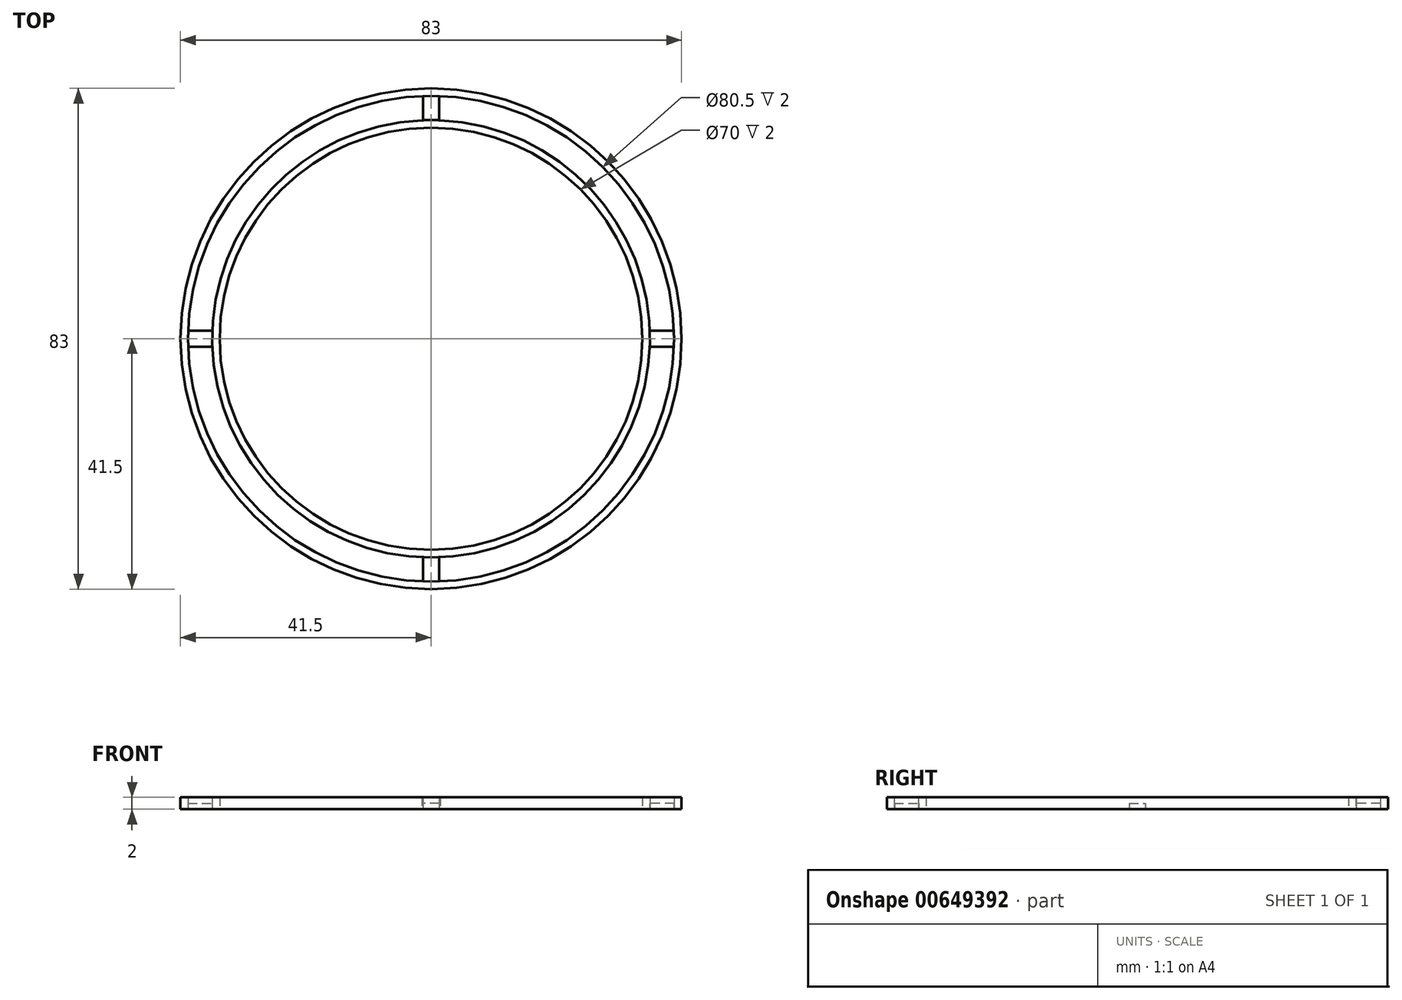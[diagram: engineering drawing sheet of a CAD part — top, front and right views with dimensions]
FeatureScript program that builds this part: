
annotation { "Feature Type Name" : "Feature", "Feature Type Description" : "" }
export const myFeature = defineFeature(function(context is Context, id is Id, definition is map)
    precondition{}
    {
        {
            var Q0;
            Q0=qCreatedBy(makeId("Top.planeOp"),FACE);
            var sketch = newSketch(context, id + "F0", { "sketchPlane" : qUnion([Q0])});
            skCircle(sketch, "E0", {"center": v(0, 0) * mm, "radius": 35 * mm});
            skCircle(sketch, "E1", {"center": v(0, 0) * mm, "radius": 36.25 * mm});
            skCircle(sketch, "E2", {"center": v(0, 0) * mm, "radius": 40.25 * mm});
            skCircle(sketch, "E3", {"center": v(0, 0) * mm, "radius": 41.5 * mm});
            skLineSegment(sketch, "E4.bottom", {"start": v(-1.52, 36.22) * mm, "end": v(1.61, 36.22) * mm});
            skLineSegment(sketch, "E4.top", {"start": v(-1.52, 41.47) * mm, "end": v(1.61, 41.47) * mm});
            skLineSegment(sketch, "E5.bottom", {"start": v(-1.33, 40.88) * mm, "end": v(1.33, 40.88) * mm});
            skLineSegment(sketch, "E5.top", {"start": v(-1.33, 35.2) * mm, "end": v(1.33, 35.2) * mm});
            skLineSegment(sketch, "E5.left", {"start": v(-1.33, 40.88) * mm, "end": v(-1.33, 35.2) * mm});
            skLineSegment(sketch, "E5.right", {"start": v(1.33, 40.88) * mm, "end": v(1.33, 35.2) * mm});
            skPoint(sketch, "E5.middle", {"position": v(0, 38.04) * mm});
            skLineSegment(sketch, "E6.1.0", {"start": v(-40.88, -1.33) * mm, "end": v(-35.2, -1.33) * mm});
            skLineSegment(sketch, "E6.1.1", {"start": v(-40.88, 1.33) * mm, "end": v(-35.2, 1.33) * mm});
            skLineSegment(sketch, "E6.1.2", {"start": v(-40.88, -1.33) * mm, "end": v(-40.88, 1.33) * mm});
            skLineSegment(sketch, "E6.1.3", {"start": v(-35.2, -1.33) * mm, "end": v(-35.2, 1.33) * mm});
            skLineSegment(sketch, "E6.2.0", {"start": v(1.33, -40.88) * mm, "end": v(1.33, -35.2) * mm});
            skLineSegment(sketch, "E6.2.1", {"start": v(-1.33, -40.88) * mm, "end": v(-1.33, -35.2) * mm});
            skLineSegment(sketch, "E6.2.2", {"start": v(1.33, -40.88) * mm, "end": v(-1.33, -40.88) * mm});
            skLineSegment(sketch, "E6.2.3", {"start": v(1.33, -35.2) * mm, "end": v(-1.33, -35.2) * mm});
            skLineSegment(sketch, "E6.3.0", {"start": v(40.88, 1.33) * mm, "end": v(35.2, 1.33) * mm});
            skLineSegment(sketch, "E6.3.1", {"start": v(40.88, -1.33) * mm, "end": v(35.2, -1.33) * mm});
            skLineSegment(sketch, "E6.3.2", {"start": v(40.88, 1.33) * mm, "end": v(40.88, -1.33) * mm});
            skLineSegment(sketch, "E6.3.3", {"start": v(35.2, 1.33) * mm, "end": v(35.2, -1.33) * mm});
            skSolve(sketch);
        }
        {
            var Q0;
            Q0=makeQuery(id+"F0.imprint","IMPRINT",FACE,{"disambiguationData":[TD([[makeQuery(id+"F0.imprint","IMPRINT",EDGE,{"derivedFrom":sQuery(id+"F0.wireOp",EDGE,"E3")}),1.0]])]});
            var Q1;
            Q1=makeQuery(id+"F0.imprint","IMPRINT",FACE,{"disambiguationData":[TD([[makeQuery(id+"F0.imprint","IMPRINT",EDGE,{"derivedFrom":sQuery(id+"F0.wireOp",EDGE,"E0")}),-1.0]])]});
            var Q2;
            {var subQ5=sQuery(id+"F0.wireOp",EDGE,"E6.1.2");Q2=makeQuery(id+"F0.imprint","IMPRINT",FACE,{"disambiguationData":[TD([[makeQuery(id+"F0.imprint","IMPRINT",EDGE,{"derivedFrom":subQ5}),-1.0]])]});}
            var Q3;
            {var subQ5=sQuery(id+"F0.wireOp",EDGE,"E6.3.3");Q3=makeQuery(id+"F0.imprint","IMPRINT",FACE,{"disambiguationData":[TD([[makeQuery(id+"F0.imprint","IMPRINT",EDGE,{"derivedFrom":subQ5}),1.0]])]});}
            var Q4;
            {var subQ5=sQuery(id+"F0.wireOp",EDGE,"E6.1.3");Q4=makeQuery(id+"F0.imprint","IMPRINT",FACE,{"disambiguationData":[TD([[makeQuery(id+"F0.imprint","IMPRINT",EDGE,{"derivedFrom":subQ5}),1.0]])]});}
            var Q5;
            {var subQ5=sQuery(id+"F0.wireOp",EDGE,"E5.bottom");Q5=makeQuery(id+"F0.imprint","IMPRINT",FACE,{"disambiguationData":[TD([[makeQuery(id+"F0.imprint","IMPRINT",EDGE,{"derivedFrom":subQ5}),-1.0]])]});}
            var Q6;
            {var subQ5=sQuery(id+"F0.wireOp",EDGE,"E6.2.3");Q6=makeQuery(id+"F0.imprint","IMPRINT",FACE,{"disambiguationData":[TD([[makeQuery(id+"F0.imprint","IMPRINT",EDGE,{"derivedFrom":subQ5}),1.0]])]});}
            var Q7;
            {var subQ5=sQuery(id+"F0.wireOp",EDGE,"E6.2.2");Q7=makeQuery(id+"F0.imprint","IMPRINT",FACE,{"disambiguationData":[TD([[makeQuery(id+"F0.imprint","IMPRINT",EDGE,{"derivedFrom":subQ5}),-1.0]])]});}
            var Q8;
            {var subQ5=sQuery(id+"F0.wireOp",EDGE,"E5.top");Q8=makeQuery(id+"F0.imprint","IMPRINT",FACE,{"disambiguationData":[TD([[makeQuery(id+"F0.imprint","IMPRINT",EDGE,{"derivedFrom":subQ5}),1.0]])]});}
            var Q9;
            {var subQ5=sQuery(id+"F0.wireOp",EDGE,"E6.3.2");Q9=makeQuery(id+"F0.imprint","IMPRINT",FACE,{"disambiguationData":[TD([[makeQuery(id+"F0.imprint","IMPRINT",EDGE,{"derivedFrom":subQ5}),-1.0]])]});}
            var Q10;
            {var subQ0=sQuery(id+"F0.wireOp",EDGE,"E5.right");var subQ1=sQuery(id+"F0.wireOp",EDGE,"E1");var subQ2=makeQuery(id+"F0.imprint","INTERSECT",VERTEX,{"derivedFrom":[subQ1,subQ0]});Q10=makeQuery(id+"F0.imprint","IMPRINT",FACE,{"disambiguationData":[TD([[makeQuery(id+"F0.imprint","IMPRINT",EDGE,{"disambiguationData":[TD([[subQ2,-1.0]])],"derivedFrom":subQ1}),1.0]])]});}
            var Q11;
            {var subQ0=sQuery(id+"F0.wireOp",EDGE,"E4.bottom");var subQ1=sQuery(id+"F0.wireOp",EDGE,"E1");var subQ2=makeQuery(id+"F0.imprint","INTERSECT",VERTEX,{"disambiguationData":[OD(0.0)],"derivedFrom":[subQ1,subQ0]});Q11=makeQuery(id+"F0.imprint","IMPRINT",FACE,{"disambiguationData":[TD([[makeQuery(id+"F0.imprint","IMPRINT",EDGE,{"disambiguationData":[TD([[subQ2,1.0]])],"derivedFrom":subQ1}),1.0]])]});}
            var Q12;
            {var subQ0=sQuery(id+"F0.wireOp",EDGE,"E4.bottom");var subQ1=sQuery(id+"F0.wireOp",EDGE,"E1");var subQ2=makeQuery(id+"F0.imprint","INTERSECT",VERTEX,{"disambiguationData":[OD(1.0)],"derivedFrom":[subQ1,subQ0]});Q12=makeQuery(id+"F0.imprint","IMPRINT",FACE,{"disambiguationData":[TD([[makeQuery(id+"F0.imprint","IMPRINT",EDGE,{"disambiguationData":[TD([[subQ2,-1.0]])],"derivedFrom":subQ1}),1.0]])]});}
            extrude(context, id + "F1", {"entities" : qUnion([Q0, Q1, Q2, Q3, Q4, Q5, Q6, Q7, Q8, Q9, Q10, Q11, Q12]), "depth" : 2 * mm, "offsetDistance" : 25 * mm});
        }
        {
            var Q0;
            {var subQ0=sQuery(id+"F0.wireOp",EDGE,"E5.right");var subQ1=sQuery(id+"F0.wireOp",EDGE,"E1");var subQ2=makeQuery(id+"F0.imprint","INTERSECT",VERTEX,{"derivedFrom":[subQ1,subQ0]});Q0=makeQuery(id+"F0.imprint","IMPRINT",FACE,{"disambiguationData":[TD([[makeQuery(id+"F0.imprint","IMPRINT",EDGE,{"disambiguationData":[TD([[subQ2,-1.0]])],"derivedFrom":subQ1}),-1.0]])]});}
            var Q1;
            {var subQ0=sQuery(id+"F0.wireOp",EDGE,"E6.3.0");var subQ1=sQuery(id+"F0.wireOp",EDGE,"E1");var subQ2=makeQuery(id+"F0.imprint","INTERSECT",VERTEX,{"derivedFrom":[subQ1,subQ0]});Q1=makeQuery(id+"F0.imprint","IMPRINT",FACE,{"disambiguationData":[TD([[makeQuery(id+"F0.imprint","IMPRINT",EDGE,{"disambiguationData":[TD([[subQ2,1.0]])],"derivedFrom":subQ1}),-1.0]])]});}
            var Q2;
            {var subQ0=sQuery(id+"F0.wireOp",EDGE,"E6.2.1");var subQ1=sQuery(id+"F0.wireOp",EDGE,"E1");var subQ2=makeQuery(id+"F0.imprint","INTERSECT",VERTEX,{"derivedFrom":[subQ1,subQ0]});Q2=makeQuery(id+"F0.imprint","IMPRINT",FACE,{"disambiguationData":[TD([[makeQuery(id+"F0.imprint","IMPRINT",EDGE,{"disambiguationData":[TD([[subQ2,-1.0]])],"derivedFrom":subQ1}),-1.0]])]});}
            var Q3;
            {var subQ0=sQuery(id+"F0.wireOp",EDGE,"E6.1.1");var subQ1=sQuery(id+"F0.wireOp",EDGE,"E1");var subQ2=makeQuery(id+"F0.imprint","INTERSECT",VERTEX,{"derivedFrom":[subQ1,subQ0]});Q3=makeQuery(id+"F0.imprint","IMPRINT",FACE,{"disambiguationData":[TD([[makeQuery(id+"F0.imprint","IMPRINT",EDGE,{"disambiguationData":[TD([[subQ2,-1.0]])],"derivedFrom":subQ1}),-1.0]])]});}
            extrude(context, id + "F2", {"entities" : qUnion([Q0, Q1, Q2, Q3]), "depth" : 1 * mm, "offsetDistance" : 25 * mm});
        }
    });
